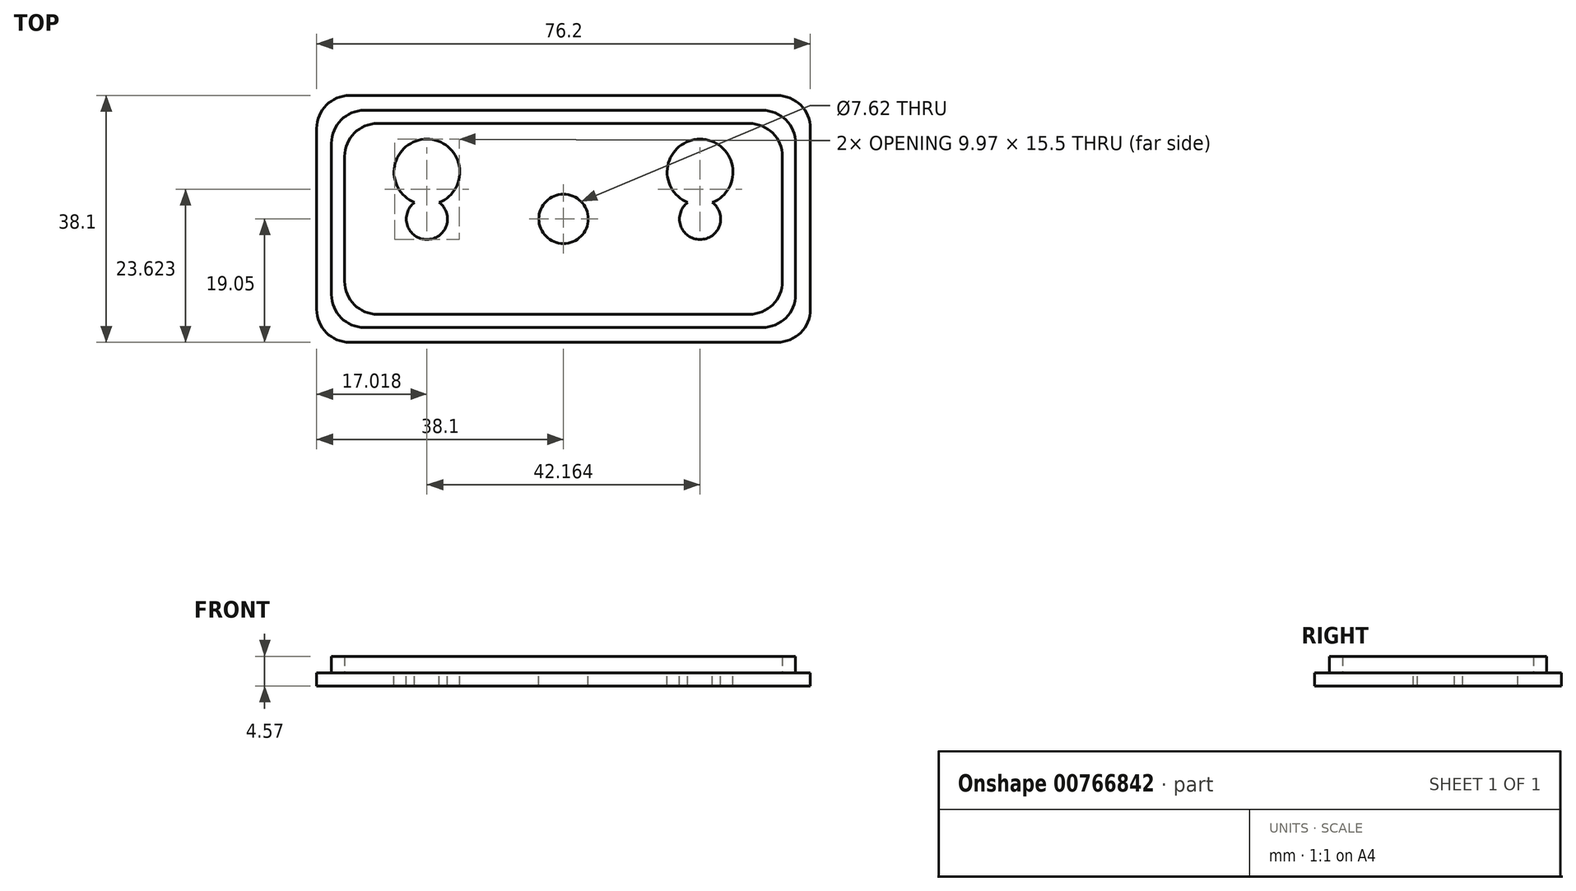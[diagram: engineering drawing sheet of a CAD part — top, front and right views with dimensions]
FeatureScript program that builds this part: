
annotation { "Feature Type Name" : "Feature", "Feature Type Description" : "" }
export const myFeature = defineFeature(function(context is Context, id is Id, definition is map)
    precondition{}
    {
        {
            var Q0;
            Q0=qCreatedBy(makeId("Top.planeOp"),FACE);
            var sketch = newSketch(context, id + "F0", { "sketchPlane" : qUnion([Q0])});
            skLineSegment(sketch, "E0.bottom", {"start": v(38.1, -19.05) * mm, "end": v(-38.1, -19.05) * mm});
            skLineSegment(sketch, "E0.top", {"start": v(38.1, 19.05) * mm, "end": v(-38.1, 19.05) * mm});
            skLineSegment(sketch, "E0.left", {"start": v(38.1, -19.05) * mm, "end": v(38.1, 19.05) * mm});
            skLineSegment(sketch, "E0.right", {"start": v(-38.1, -19.05) * mm, "end": v(-38.1, 19.05) * mm});
            skPoint(sketch, "E0.middle", {"position": v(0, 0) * mm});
            skSolve(sketch);
        }
        {
            var Q0;
            Q0=makeQuery(id+"F0.imprint","IMPRINT",FACE,{"disambiguationData":[TD([[makeQuery(id+"F0.imprint","IMPRINT",EDGE,{"derivedFrom":sQuery(id+"F0.wireOp",EDGE,"E0.bottom")}),-1.0]])]});
            extrude(context, id + "F1", {"entities" : qUnion([Q0]), "depth" : 2.03 * mm, "offsetDistance" : 25.4 * mm});
        }
        {
            var Q0;
            Q0=makeQuery(id+"F1.opExtrude","CAP_FACE",FACE,{"disambiguationData":[OSD([sQuery(id+"F0.wireOp",EDGE,"E0.bottom"),sQuery(id+"F0.wireOp",EDGE,"E0.top"),sQuery(id+"F0.wireOp",EDGE,"E0.left"),sQuery(id+"F0.wireOp",EDGE,"E0.right")])],"isStart":false});
            var sketch = newSketch(context, id + "F2", { "sketchPlane" : qUnion([Q0])});
            skLineSegment(sketch, "E1.bottom", {"start": v(35.81, 16.76) * mm, "end": v(-35.81, 16.76) * mm});
            skLineSegment(sketch, "E1.top", {"start": v(35.81, -16.76) * mm, "end": v(-35.81, -16.76) * mm});
            skLineSegment(sketch, "E1.left", {"start": v(35.81, 16.76) * mm, "end": v(35.81, -16.76) * mm});
            skLineSegment(sketch, "E1.right", {"start": v(-35.81, 16.76) * mm, "end": v(-35.81, -16.76) * mm});
            skPoint(sketch, "E1.middle", {"position": v(0, 0) * mm});
            skLineSegment(sketch, "E2.bottom", {"start": v(33.78, 14.73) * mm, "end": v(-33.78, 14.73) * mm});
            skLineSegment(sketch, "E2.top", {"start": v(33.78, -14.73) * mm, "end": v(-33.78, -14.73) * mm});
            skLineSegment(sketch, "E2.left", {"start": v(33.78, 14.73) * mm, "end": v(33.78, -14.73) * mm});
            skLineSegment(sketch, "E2.right", {"start": v(-33.78, 14.73) * mm, "end": v(-33.78, -14.73) * mm});
            skCircle(sketch, "E3", {"center": v(0, 0) * mm, "radius": 3.81 * mm});
            skSolve(sketch);
        }
        {
            var Q0;
            Q0=makeQuery(id+"F2.imprint","IMPRINT",FACE,{"disambiguationData":[TD([[makeQuery(id+"F2.imprint","IMPRINT",EDGE,{"derivedFrom":sQuery(id+"F2.wireOp",EDGE,"E3")}),1.0]])]});
            extrude(context, id + "F3", {"entities" : qUnion([Q0]), "operationType" : NewBodyOperationType.REMOVE, "oppositeDirection" : true, "depth" : 25.4 * mm, "offsetDistance" : 25.4 * mm});
        }
        {
            var Q0;
            Q0=makeQuery(id+"F2.imprint","IMPRINT",FACE,{"disambiguationData":[TD([[makeQuery(id+"F2.imprint","IMPRINT",EDGE,{"derivedFrom":sQuery(id+"F2.wireOp",EDGE,"E1.bottom")}),1.0]])]});
            extrude(context, id + "F4", {"entities" : qUnion([Q0]), "operationType" : NewBodyOperationType.ADD, "depth" : 2.54 * mm, "offsetDistance" : 25.4 * mm});
        }
        {
            var Q0;
            Q0=makeQuery(id+"F4.opExtrude","SWEPT_EDGE",EDGE,{"disambiguationData":[OSD([sQuery(id+"F2.wireOp",EDGE,"E2.bottom"),sQuery(id+"F2.wireOp",EDGE,"E2.right")])]});
            var Q1;
            Q1=makeQuery(id+"F4.opExtrude","SWEPT_EDGE",EDGE,{"disambiguationData":[OSD([sQuery(id+"F2.wireOp",EDGE,"E2.top"),sQuery(id+"F2.wireOp",EDGE,"E2.right")])]});
            var Q2;
            Q2=makeQuery(id+"F4.opExtrude","SWEPT_EDGE",EDGE,{"disambiguationData":[OSD([sQuery(id+"F2.wireOp",EDGE,"E2.top"),sQuery(id+"F2.wireOp",EDGE,"E2.left")])]});
            var Q3;
            Q3=makeQuery(id+"F4.opExtrude","SWEPT_EDGE",EDGE,{"disambiguationData":[OSD([sQuery(id+"F2.wireOp",EDGE,"E2.bottom"),sQuery(id+"F2.wireOp",EDGE,"E2.left")])]});
            var Q4;
            Q4=makeQuery(id+"F4.opExtrude","SWEPT_EDGE",EDGE,{"disambiguationData":[OSD([sQuery(id+"F2.wireOp",EDGE,"E1.top"),sQuery(id+"F2.wireOp",EDGE,"E1.right")])]});
            var Q5;
            Q5=makeQuery(id+"F1.opExtrude","SWEPT_EDGE",EDGE,{"disambiguationData":[OSD([sQuery(id+"F0.wireOp",EDGE,"E0.bottom"),sQuery(id+"F0.wireOp",EDGE,"E0.right")])]});
            var Q6;
            Q6=makeQuery(id+"F1.opExtrude","SWEPT_EDGE",EDGE,{"disambiguationData":[OSD([sQuery(id+"F0.wireOp",EDGE,"E0.bottom"),sQuery(id+"F0.wireOp",EDGE,"E0.left")])]});
            var Q7;
            Q7=makeQuery(id+"F4.opExtrude","SWEPT_EDGE",EDGE,{"disambiguationData":[OSD([sQuery(id+"F2.wireOp",EDGE,"E1.top"),sQuery(id+"F2.wireOp",EDGE,"E1.left")])]});
            var Q8;
            Q8=makeQuery(id+"F1.opExtrude","SWEPT_EDGE",EDGE,{"disambiguationData":[OSD([sQuery(id+"F0.wireOp",EDGE,"E0.top"),sQuery(id+"F0.wireOp",EDGE,"E0.left")])]});
            var Q9;
            Q9=makeQuery(id+"F4.opExtrude","SWEPT_EDGE",EDGE,{"disambiguationData":[OSD([sQuery(id+"F2.wireOp",EDGE,"E1.bottom"),sQuery(id+"F2.wireOp",EDGE,"E1.left")])]});
            var Q10;
            Q10=makeQuery(id+"F4.opExtrude","SWEPT_EDGE",EDGE,{"disambiguationData":[OSD([sQuery(id+"F2.wireOp",EDGE,"E1.bottom"),sQuery(id+"F2.wireOp",EDGE,"E1.right")])]});
            var Q11;
            Q11=makeQuery(id+"F1.opExtrude","SWEPT_EDGE",EDGE,{"disambiguationData":[OSD([sQuery(id+"F0.wireOp",EDGE,"E0.top"),sQuery(id+"F0.wireOp",EDGE,"E0.right")])]});
            fillet(context, id + "F5", {"entities" : qUnion([Q0, Q1, Q2, Q3, Q4, Q5, Q6, Q7, Q8, Q9, Q10, Q11]), "radius" : 5.08 * mm, "tangentPropagation" : true, "allowEdgeOverflow" : false});
        }
        {
            var Q0;
            Q0=makeQuery(id+"F2.imprint","IMPRINT",FACE,{"disambiguationData":[TD([[makeQuery(id+"F2.imprint","IMPRINT",EDGE,{"derivedFrom":sQuery(id+"F2.wireOp",EDGE,"E2.bottom")}),1.0]])]});
            var sketch = newSketch(context, id + "F6", { "sketchPlane" : qUnion([Q0])});
            skLineSegment(sketch, "E4", {"start": v(23.77, 0) * mm, "end": v(-23.8, 0) * mm, "construction": true});
            skLineSegment(sketch, "E5", {"start": v(21.08, -10.66) * mm, "end": v(21.08, 10.7) * mm, "construction": true});
            skLineSegment(sketch, "E6", {"start": v(-21.08, -10.51) * mm, "end": v(-21.08, 10.54) * mm, "construction": true});
            skCircle(sketch, "E7", {"center": v(21.08, 0) * mm, "radius": 3.18 * mm});
            skCircle(sketch, "E8", {"center": v(-21.08, 0) * mm, "radius": 3.18 * mm});
            skLineSegment(sketch, "E9", {"start": v(30.78, 7.24) * mm, "end": v(-30.62, 7.24) * mm, "construction": true});
            skCircle(sketch, "E10", {"center": v(21.08, 7.24) * mm, "radius": 5.08 * mm});
            skCircle(sketch, "E11", {"center": v(-21.08, 7.24) * mm, "radius": 5.08 * mm});
            skLineSegment(sketch, "E12", {"start": v(24.26, 0) * mm, "end": v(24.26, 7.24) * mm});
            skLineSegment(sketch, "E13", {"start": v(17.9, 0) * mm, "end": v(17.9, 7.24) * mm});
            skLineSegment(sketch, "E14", {"start": v(-17.9, 0) * mm, "end": v(-17.9, 7.24) * mm});
            skLineSegment(sketch, "E15", {"start": v(-24.26, 0) * mm, "end": v(-24.26, 7.24) * mm});
            skLineSegment(sketch, "E16", {"start": v(24.26, 0) * mm, "end": v(24.26, 3.27) * mm});
            skLineSegment(sketch, "E17", {"start": v(17.9, 0) * mm, "end": v(17.9, 3.27) * mm});
            skLineSegment(sketch, "E18", {"start": v(-17.9, 0) * mm, "end": v(-17.9, 3.27) * mm});
            skLineSegment(sketch, "E19", {"start": v(-24.26, 0) * mm, "end": v(-24.26, 3.27) * mm});
            skSolve(sketch);
        }
        {
            var Q0;
            {var subQ0=sQuery(id+"F6.wireOp",EDGE,"E10");var subQ1=sQuery(id+"F6.wireOp",EDGE,"E7");var subQ2=makeQuery(id+"F6.imprint","INTERSECT",VERTEX,{"disambiguationData":[OD(0.0)],"derivedFrom":[subQ1,subQ0]});Q0=makeQuery(id+"F6.imprint","IMPRINT",FACE,{"disambiguationData":[TD([[makeQuery(id+"F6.imprint","IMPRINT",EDGE,{"disambiguationData":[TD([[subQ2,-1.0]])],"derivedFrom":subQ1}),1.0]])]});}
            var Q1;
            {var subQ0=sQuery(id+"F6.wireOp",EDGE,"E7");var subQ1=makeQuery(id+"F6.imprint","INTERSECT",VERTEX,{"derivedFrom":[subQ0,sQuery(id+"F6.wireOp",EDGE,"E16")]});Q1=makeQuery(id+"F6.imprint","IMPRINT",FACE,{"disambiguationData":[TD([[makeQuery(id+"F6.imprint","IMPRINT",EDGE,{"disambiguationData":[TD([[subQ1,-1.0]])],"derivedFrom":subQ0}),1.0]])]});}
            var Q2;
            {var subQ0=sQuery(id+"F6.wireOp",EDGE,"E10");var subQ1=sQuery(id+"F6.wireOp",EDGE,"E7");var subQ2=makeQuery(id+"F6.imprint","INTERSECT",VERTEX,{"disambiguationData":[OD(0.0)],"derivedFrom":[subQ1,subQ0]});Q2=makeQuery(id+"F6.imprint","IMPRINT",FACE,{"disambiguationData":[TD([[makeQuery(id+"F6.imprint","IMPRINT",EDGE,{"disambiguationData":[TD([[subQ2,-1.0]])],"derivedFrom":subQ1}),-1.0]])]});}
            var Q3;
            {var subQ0=sQuery(id+"F6.wireOp",EDGE,"E17");Q3=makeQuery(id+"F6.imprint","IMPRINT",FACE,{"disambiguationData":[TD([[makeQuery(id+"F6.imprint","IMPRINT",EDGE,{"derivedFrom":subQ0}),-1.0]])]});}
            var Q4;
            {var subQ0=sQuery(id+"F6.wireOp",EDGE,"E16");Q4=makeQuery(id+"F6.imprint","IMPRINT",FACE,{"disambiguationData":[TD([[makeQuery(id+"F6.imprint","IMPRINT",EDGE,{"derivedFrom":subQ0}),1.0]])]});}
            extrude(context, id + "F7", {"entities" : qUnion([Q0, Q1, Q2, Q3, Q4]), "operationType" : NewBodyOperationType.REMOVE, "oppositeDirection" : true, "depth" : 25.4 * mm, "offsetDistance" : 25.4 * mm});
        }
        {
            var Q0;
            {var subQ0=sQuery(id+"F6.wireOp",EDGE,"E11");var subQ1=sQuery(id+"F6.wireOp",EDGE,"E8");var subQ2=makeQuery(id+"F6.imprint","INTERSECT",VERTEX,{"disambiguationData":[OD(0.0)],"derivedFrom":[subQ1,subQ0]});Q0=makeQuery(id+"F6.imprint","IMPRINT",FACE,{"disambiguationData":[TD([[makeQuery(id+"F6.imprint","IMPRINT",EDGE,{"disambiguationData":[TD([[subQ2,-1.0]])],"derivedFrom":subQ1}),-1.0]])]});}
            var Q1;
            {var subQ0=sQuery(id+"F6.wireOp",EDGE,"E8");var subQ1=makeQuery(id+"F6.imprint","INTERSECT",VERTEX,{"derivedFrom":[subQ0,sQuery(id+"F6.wireOp",EDGE,"E18")]});Q1=makeQuery(id+"F6.imprint","IMPRINT",FACE,{"disambiguationData":[TD([[makeQuery(id+"F6.imprint","IMPRINT",EDGE,{"disambiguationData":[TD([[subQ1,-1.0]])],"derivedFrom":subQ0}),1.0]])]});}
            var Q2;
            {var subQ0=sQuery(id+"F6.wireOp",EDGE,"E19");Q2=makeQuery(id+"F6.imprint","IMPRINT",FACE,{"disambiguationData":[TD([[makeQuery(id+"F6.imprint","IMPRINT",EDGE,{"derivedFrom":subQ0}),-1.0]])]});}
            var Q3;
            {var subQ0=sQuery(id+"F6.wireOp",EDGE,"E11");var subQ1=sQuery(id+"F6.wireOp",EDGE,"E8");var subQ2=makeQuery(id+"F6.imprint","INTERSECT",VERTEX,{"disambiguationData":[OD(0.0)],"derivedFrom":[subQ1,subQ0]});Q3=makeQuery(id+"F6.imprint","IMPRINT",FACE,{"disambiguationData":[TD([[makeQuery(id+"F6.imprint","IMPRINT",EDGE,{"disambiguationData":[TD([[subQ2,-1.0]])],"derivedFrom":subQ1}),1.0]])]});}
            var Q4;
            {var subQ0=sQuery(id+"F6.wireOp",EDGE,"E18");Q4=makeQuery(id+"F6.imprint","IMPRINT",FACE,{"disambiguationData":[TD([[makeQuery(id+"F6.imprint","IMPRINT",EDGE,{"derivedFrom":subQ0}),1.0]])]});}
            extrude(context, id + "F8", {"entities" : qUnion([Q0, Q1, Q2, Q3, Q4]), "operationType" : NewBodyOperationType.REMOVE, "oppositeDirection" : true, "depth" : 25.4 * mm, "offsetDistance" : 25.4 * mm});
        }
    });
